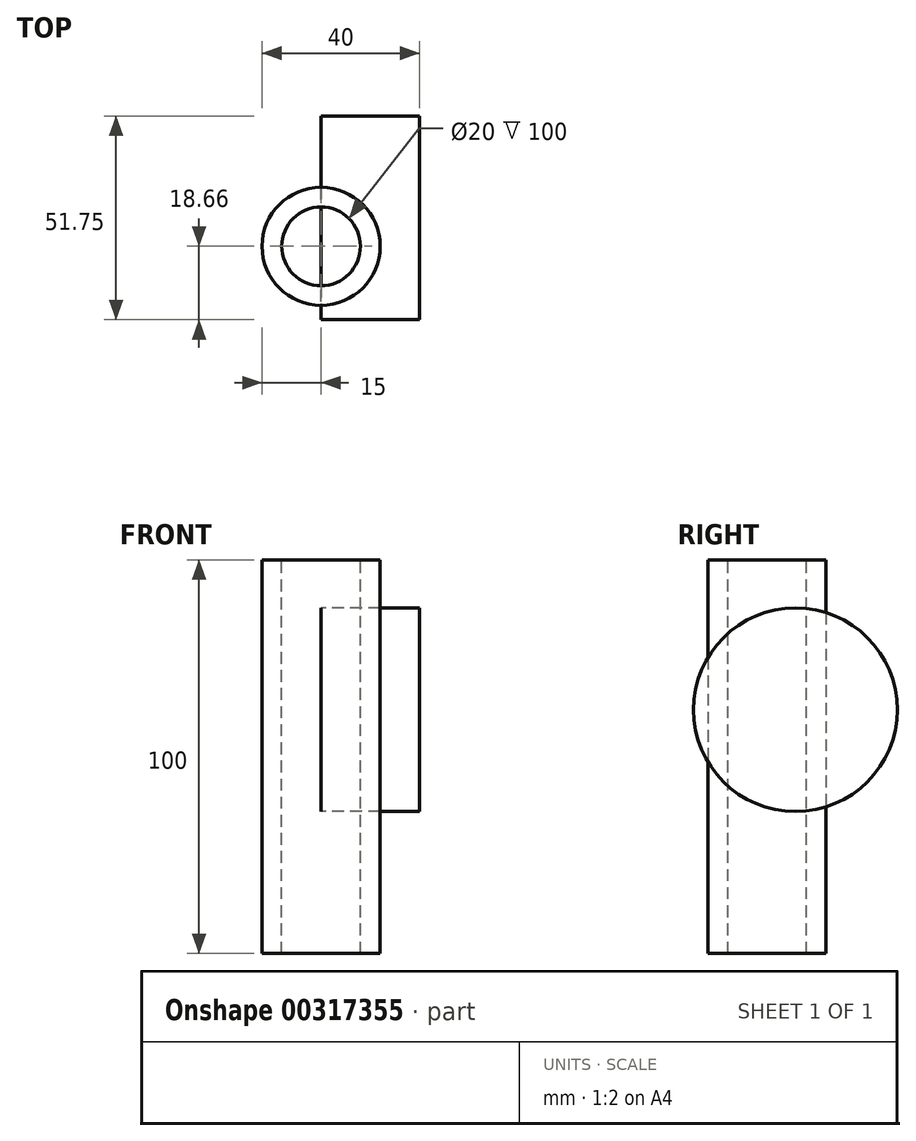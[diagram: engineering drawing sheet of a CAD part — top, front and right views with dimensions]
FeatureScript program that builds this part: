
annotation { "Feature Type Name" : "Feature", "Feature Type Description" : "" }
export const myFeature = defineFeature(function(context is Context, id is Id, definition is map)
    precondition{}
    {
        {
            var Q0;
            Q0=qCreatedBy(makeId("Top.planeOp"),FACE);
            var sketch = newSketch(context, id + "F0", { "sketchPlane" : qUnion([Q0])});
            skCircle(sketch, "E0", {"center": v(0, 0) * mm, "radius": 15 * mm});
            skSolve(sketch);
        }
        {
            var Q0;
            Q0=makeQuery(id+"F0.imprint","IMPRINT",FACE,{"disambiguationData":[TD([[makeQuery(id+"F0.imprint","IMPRINT",EDGE,{"derivedFrom":sQuery(id+"F0.wireOp",EDGE,"E0")}),1.0]])]});
            var Q1;
            Q1=sQuery(id+"F0.wireOp",EDGE,"E0");
            extrude(context, id + "F1", {"entities" : qUnion([Q0]), "surfaceEntities" : qUnion([Q1]), "depth" : 100 * mm});
        }
        {
            var Q0;
            Q0=makeQuery(id+"F1.opExtrude","CAP_FACE",FACE,{"disambiguationData":[OSD([sQuery(id+"F0.wireOp",EDGE,"E0")])],"isStart":false});
            var sketch = newSketch(context, id + "F2", { "sketchPlane" : qUnion([Q0])});
            skSolve(sketch);
        }
        {
            var Q0;
            Q0=makeQuery(id+"F2.imprint","IMPRINT",FACE,{"disambiguationData":[TD([[makeQuery(id+"F2.imprint","IMPRINT",EDGE,{"derivedFrom":makeQuery(id+"F1.opExtrude","CAP_EDGE",EDGE,{"disambiguationData":[OSD([sQuery(id+"F0.wireOp",EDGE,"E0")])],"isStart":false})}),1.0]])]});
            var sketch = newSketch(context, id + "F3", { "sketchPlane" : qUnion([Q0])});
            skCircle(sketch, "E1", {"center": v(0, 0) * mm, "radius": 10 * mm});
            skSolve(sketch);
        }
        {
            var Q0;
            Q0=makeQuery(id+"F3.imprint","IMPRINT",FACE,{"disambiguationData":[TD([[makeQuery(id+"F3.imprint","IMPRINT",EDGE,{"derivedFrom":sQuery(id+"F3.wireOp",EDGE,"E1")}),1.0]])]});
            var Q1;
            Q1=sQuery(id+"F3.wireOp",EDGE,"E1");
            extrude(context, id + "F4", {"entities" : qUnion([Q0]), "operationType" : NewBodyOperationType.REMOVE, "surfaceEntities" : qUnion([Q1]), "endBound" : BoundingType.UP_TO_NEXT, "oppositeDirection" : true, "depth" : 61.3 * mm});
        }
        {
            var Q0;
            Q0=qCreatedBy(makeId("Right.planeOp"),FACE);
            var sketch = newSketch(context, id + "F5", { "sketchPlane" : qUnion([Q0])});
            skCircle(sketch, "E2", {"center": v(7.22, 61.92) * mm, "radius": 25.87 * mm});
            skSolve(sketch);
        }
        {
            var Q0;
            Q0=makeQuery(id+"F5.imprint","IMPRINT",FACE,{"disambiguationData":[TD([[makeQuery(id+"F5.imprint","IMPRINT",EDGE,{"derivedFrom":sQuery(id+"F5.wireOp",EDGE,"E2")}),1.0]])]});
            var Q1;
            Q1=sQuery(id+"F5.wireOp",EDGE,"E2");
            extrude(context, id + "F6", {"entities" : qUnion([Q0]), "surfaceEntities" : qUnion([Q1]), "offsetDistance" : 25 * mm, "depth" : 25 * mm});
        }
    });
